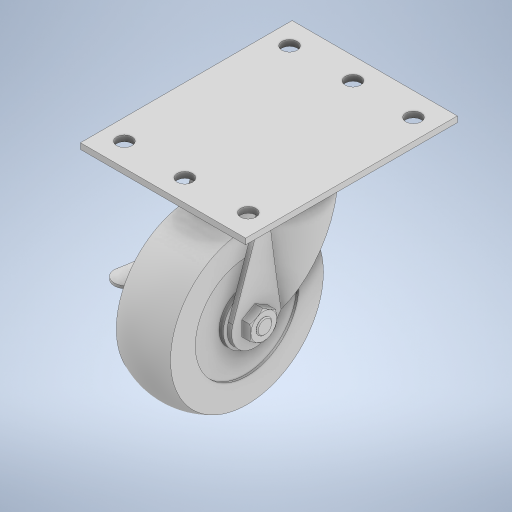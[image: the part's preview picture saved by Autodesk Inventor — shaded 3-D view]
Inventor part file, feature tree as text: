
AUTODESK INVENTOR PART (.ipt)
format: ipt  version: 2024 (Build 280153000, 153)  size: 423,424 bytes
history: native  units: in
note: dims shown in document units (in); Inventor stores cm internally (conversion verified against a paired STEP export)
features: boolean_combine x2, extrude x1, sketch x1, projected_geometry x1, revolve x1
ambient origin geometry x8: Origin, YZ Plane, XZ Plane, XY Plane, X Axis, Y Axis, Z Axis, Center Point
bodies: Solid1 (feature_tree), Solid2 (feature_tree), Solid3 (feature_tree)
feature tree (6):
  extrude  "Extrusion1"  Depth=1.0in
  sketch  "Sketch1"  dims[d3=0.375in d4=0.25in d5=1.0in d6=5.125in d7=0.09in d9=0.375in d10=0.25in d11=0.25in d12=0.0in]
  projected_geometry  "Projected Loop1"
  revolve  "Revolve1"  [1 undecoded]
  boolean_combine  "Combine3"
  boolean_combine  "Combine4"
note: 1 required parameter value undecoded (feature->parameter linkage not recoverable at this tier; creation-order binding heuristic only, values carry confidence <= 0.55)
